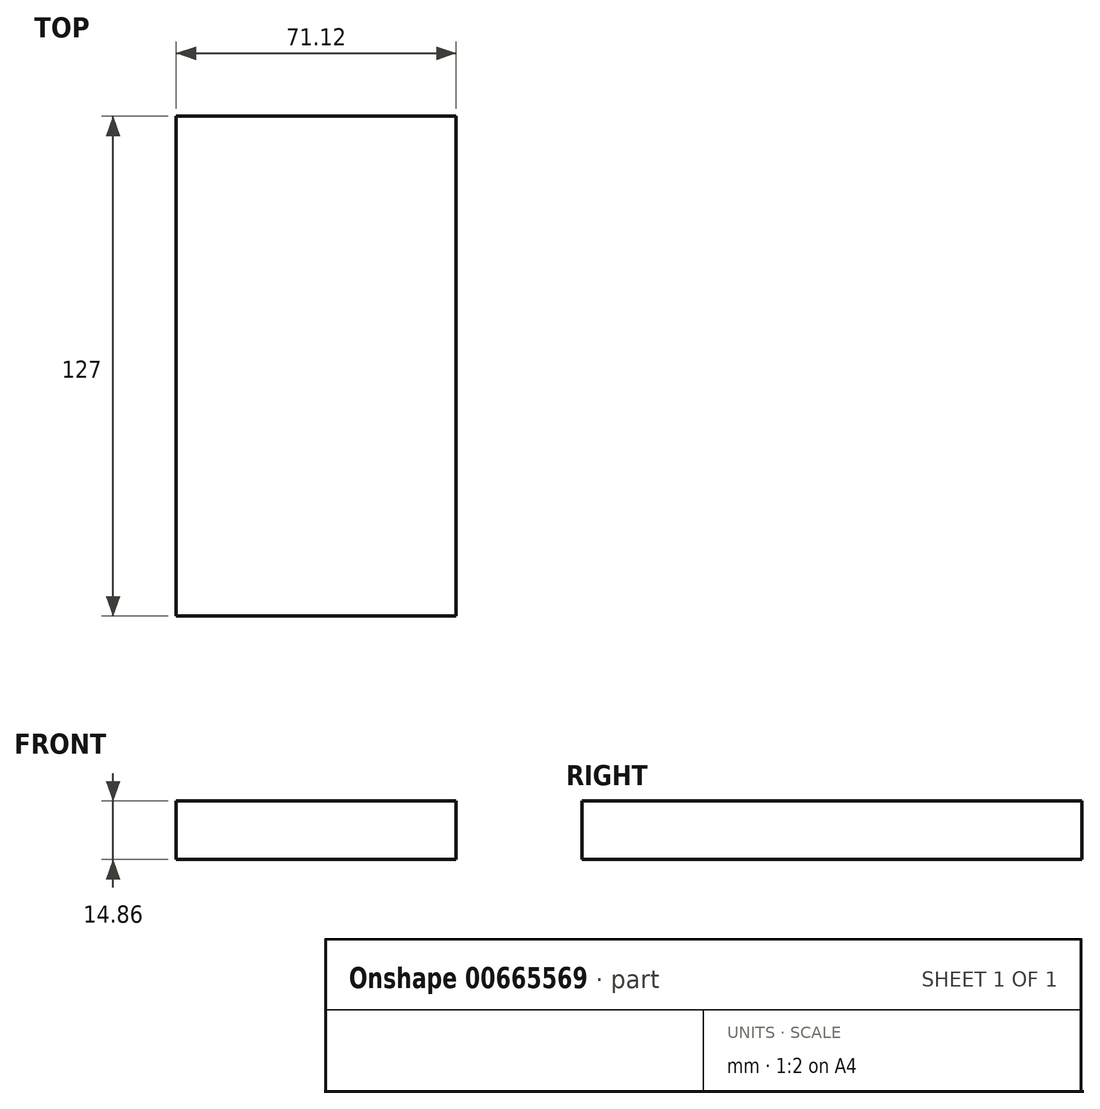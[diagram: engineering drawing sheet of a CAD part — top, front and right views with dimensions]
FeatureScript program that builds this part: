
annotation { "Feature Type Name" : "Feature", "Feature Type Description" : "" }
export const myFeature = defineFeature(function(context is Context, id is Id, definition is map)
    precondition{}
    {
        {
            var Q0;
            Q0=qCreatedBy(makeId("Front.planeOp"),FACE);
            var sketch = newSketch(context, id + "F0", { "sketchPlane" : qUnion([Q0])});
            skLineSegment(sketch, "E0.bottom", {"start": v(-35.41, 10.2) * mm, "end": v(35.7, 10.2) * mm});
            skLineSegment(sketch, "E0.top", {"start": v(-35.41, -4.66) * mm, "end": v(35.7, -4.66) * mm});
            skLineSegment(sketch, "E0.left", {"start": v(-35.41, 10.2) * mm, "end": v(-35.41, -4.66) * mm});
            skLineSegment(sketch, "E0.right", {"start": v(35.7, 10.2) * mm, "end": v(35.7, -4.66) * mm});
            skSolve(sketch);
        }
        {
            var Q0;
            Q0 = qSketchRegion(id + "F0", true);
            extrude(context, id + "F1", {"entities" : qUnion([Q0]), "endBound" : BoundingType.SYMMETRIC, "depth" : 127 * mm, "offsetDistance" : 25.4 * mm});
        }
    });
